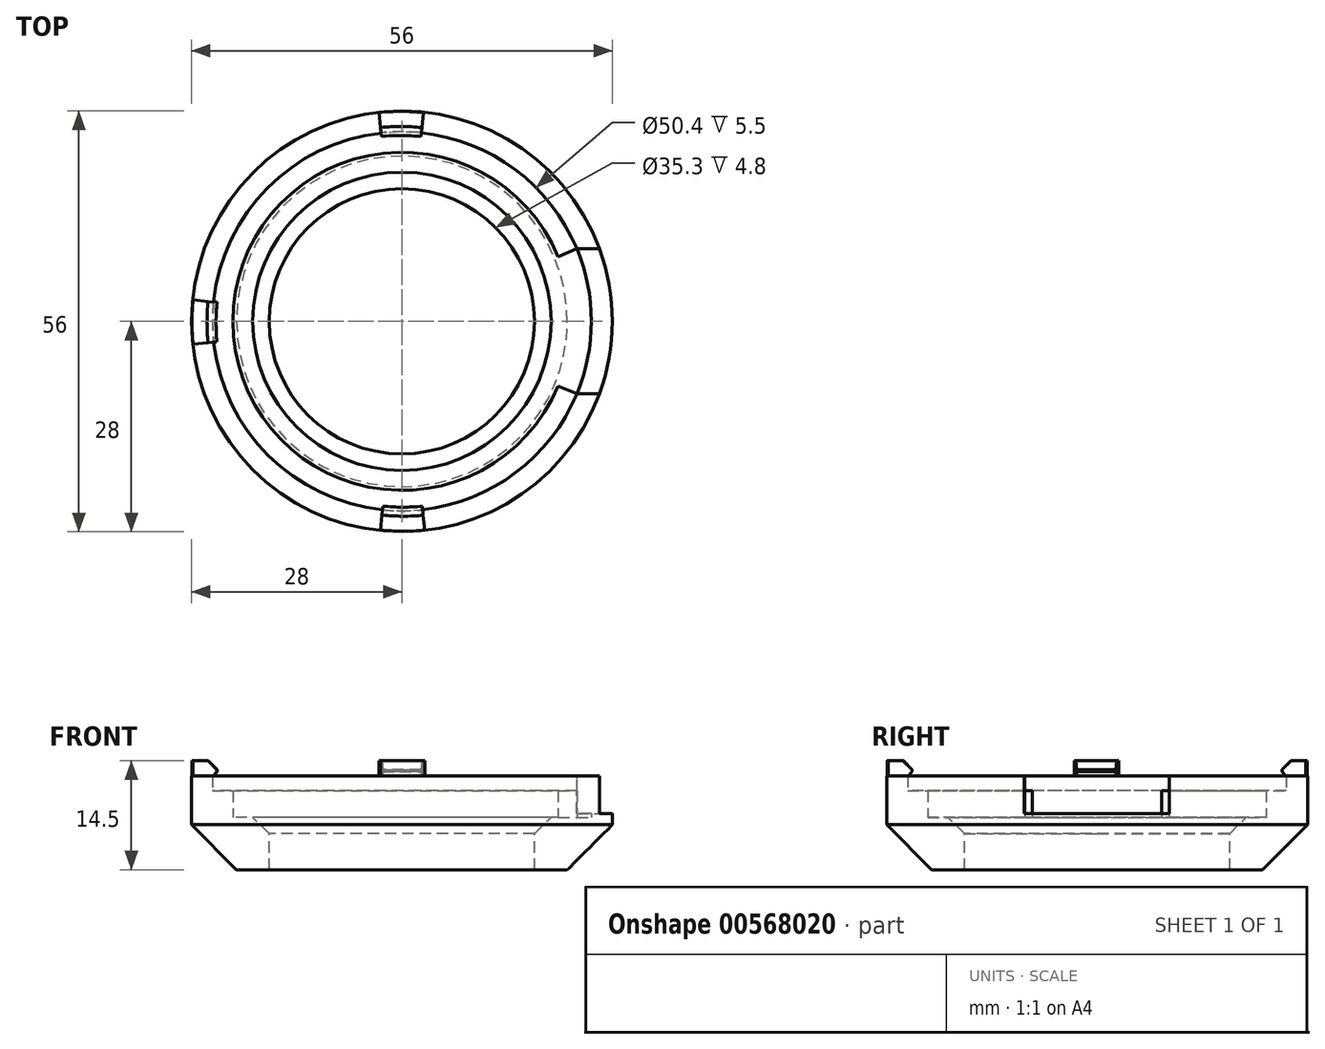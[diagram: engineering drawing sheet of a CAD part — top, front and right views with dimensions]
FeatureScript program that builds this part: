
annotation { "Feature Type Name" : "Feature", "Feature Type Description" : "" }
export const myFeature = defineFeature(function(context is Context, id is Id, definition is map)
    precondition{}
    {
        {
            var Q0;
            Q0=qCreatedBy(makeId("Top.planeOp"),FACE);
            var sketch = newSketch(context, id + "F0", { "sketchPlane" : qUnion([Q0])});
            skArc(sketch, "E0", {"start": v(23.28, 9.64) * mm, "mid": v(-25.2, 0) * mm, "end": v(23.28, -9.64) * mm});
            skArc(sketch, "E1", {"start": v(25.87, 10.72) * mm, "mid": v(-28, 0) * mm, "end": v(25.87, -10.72) * mm});
            skArc(sketch, "E2", {"start": v(16.3, 6.75) * mm, "mid": v(-17.65, 0) * mm, "end": v(16.3, -6.75) * mm});
            skLineSegment(sketch, "E3", {"start": v(0, 0) * mm, "end": v(25.87, 10.72) * mm});
            skLineSegment(sketch, "E4.MirrorCS", {"start": v(0, 0) * mm, "end": v(25.87, -10.72) * mm});
            skCircle(sketch, "E5", {"center": v(0, 0) * mm, "radius": 22.5 * mm});
            skCircle(sketch, "E6", {"center": v(0, 0) * mm, "radius": 17.65 * mm});
            skArc(sketch, "E7", {"start": v(23.28, -9.64) * mm, "mid": v(25.2, 0) * mm, "end": v(23.28, 9.64) * mm});
            skArc(sketch, "E8", {"start": v(25.87, -10.72) * mm, "mid": v(28, 0) * mm, "end": v(25.87, 10.72) * mm});
            skSolve(sketch);
        }
        {
            var Q0;
            Q0=makeQuery(id+"F0.imprint","IMPRINT",FACE,{"disambiguationData":[TD([[makeQuery(id+"F0.imprint","IMPRINT",EDGE,{"derivedFrom":sQuery(id+"F0.wireOp",EDGE,"E0")}),-1.0]])]});
            var Q1;
            {var subQ0=sQuery(id+"F0.wireOp",EDGE,"E7");Q1=makeQuery(id+"F0.imprint","IMPRINT",FACE,{"disambiguationData":[TD([[makeQuery(id+"F0.imprint","IMPRINT",EDGE,{"derivedFrom":subQ0}),-1.0]])]});}
            extrude(context, id + "F1", {"entities" : qUnion([Q0, Q1]), "depth" : 5.5 * mm, "offsetDistance" : 25 * mm, "hasSecondDirection" : true, "secondDirectionOppositeDirection" : true, "secondDirectionDepth" : 7 * mm});
        }
        {
            var Q0;
            Q0=makeQuery(id+"F0.imprint","IMPRINT",FACE,{"disambiguationData":[TD([[makeQuery(id+"F0.imprint","IMPRINT",EDGE,{"derivedFrom":sQuery(id+"F0.wireOp",EDGE,"E0")}),1.0]])]});
            var Q1;
            {var subQ0=sQuery(id+"F0.wireOp",EDGE,"E2");Q1=makeQuery(id+"F0.imprint","IMPRINT",FACE,{"disambiguationData":[TD([[makeQuery(id+"F0.imprint","IMPRINT",EDGE,{"derivedFrom":subQ0}),-1.0]])]});}
            var Q2;
            {var subQ0=sQuery(id+"F0.wireOp",EDGE,"E5");var subQ1=sQuery(id+"F0.wireOp",EDGE,"E3");var subQ2=makeQuery(id+"F0.imprint","INTERSECT",VERTEX,{"derivedFrom":[subQ1,subQ0]});Q2=makeQuery(id+"F0.imprint","IMPRINT",FACE,{"disambiguationData":[TD([[makeQuery(id+"F0.imprint","IMPRINT",EDGE,{"disambiguationData":[TD([[subQ2,1.0]])],"derivedFrom":subQ1}),-1.0]])]});}
            var Q3;
            {var subQ0=sQuery(id+"F0.wireOp",EDGE,"E5");var subQ1=sQuery(id+"F0.wireOp",EDGE,"E3");var subQ2=makeQuery(id+"F0.imprint","INTERSECT",VERTEX,{"derivedFrom":[subQ1,subQ0]});Q3=makeQuery(id+"F0.imprint","IMPRINT",FACE,{"disambiguationData":[TD([[makeQuery(id+"F0.imprint","IMPRINT",EDGE,{"disambiguationData":[TD([[subQ2,1.0]])],"derivedFrom":subQ1}),1.0]])]});}
            var Q4;
            {var subQ0=sQuery(id+"F0.wireOp",EDGE,"E7");Q4=makeQuery(id+"F0.imprint","IMPRINT",FACE,{"disambiguationData":[TD([[makeQuery(id+"F0.imprint","IMPRINT",EDGE,{"derivedFrom":subQ0}),1.0]])]});}
            extrude(context, id + "F2", {"entities" : qUnion([Q0, Q1, Q2, Q3, Q4]), "operationType" : NewBodyOperationType.ADD, "oppositeDirection" : true, "depth" : 7 * mm, "offsetDistance" : 25 * mm});
        }
        {
            var Q0;
            {var subQ0=sQuery(id+"F0.wireOp",EDGE,"E0");Q0=makeQuery(id+"F0.imprint","IMPRINT",FACE,{"disambiguationData":[TD([[makeQuery(id+"F0.imprint","IMPRINT",EDGE,{"derivedFrom":subQ0}),1.0]])]});}
            extrude(context, id + "F3", {"entities" : qUnion([Q0]), "operationType" : NewBodyOperationType.ADD, "depth" : 3.5 * mm, "offsetDistance" : 25 * mm});
        }
        {
            var Q0;
            Q0=makeQuery(id+"F1.opExtrude","CAP_EDGE",EDGE,{"disambiguationData":[OSD([sQuery(id+"F0.wireOp",EDGE,"E1")])],"isStart":true});
            chamfer(context, id + "F4", {"entities" : qUnion([Q0]), "width" : 6 * mm, "tangentPropagation" : true});
        }
        {
            var Q0;
            Q0=makeQuery(id+"F1.opExtrude","CAP_FACE",FACE,{"disambiguationData":[OSD([sQuery(id+"F0.wireOp",EDGE,"E0"),sQuery(id+"F0.wireOp",EDGE,"E1"),sQuery(id+"F0.wireOp",EDGE,"E7"),sQuery(id+"F0.wireOp",EDGE,"E8")])],"isStart":false});
            var sketch = newSketch(context, id + "F5", { "sketchPlane" : qUnion([Q0])});
            skArc(sketch, "E9", {"start": v(26.39, -9.67) * mm, "mid": v(28.15, -0.01) * mm, "end": v(26.4, 9.65) * mm});
            skLineSegment(sketch, "E10", {"start": v(23.28, 9.65) * mm, "end": v(20.75, 8.38) * mm});
            skArc(sketch, "E11", {"start": v(20.68, -8.36) * mm, "mid": v(22.33, 0) * mm, "end": v(20.75, 8.38) * mm});
            skLineSegment(sketch, "E12", {"start": v(20.68, -8.36) * mm, "end": v(23.29, -9.63) * mm});
            skLineSegment(sketch, "E13", {"start": v(23.28, 9.65) * mm, "end": v(26.4, 9.65) * mm});
            skLineSegment(sketch, "E14", {"start": v(23.29, -9.63) * mm, "end": v(26.39, -9.67) * mm});
            skSolve(sketch);
        }
        {
            var Q0;
            {var subQ0=sQuery(id+"F5.wireOp",EDGE,"E11");Q0=makeQuery(id+"F5.imprint","IMPRINT",FACE,{"disambiguationData":[TD([[makeQuery(id+"F5.imprint","IMPRINT",EDGE,{"derivedFrom":subQ0}),-1.0]])]});}
            var Q1;
            {var subQ0=sQuery(id+"F5.wireOp",EDGE,"E10");var subQ4=makeQuery(id+"F1.opExtrude","CAP_EDGE",EDGE,{"disambiguationData":[OSD([sQuery(id+"F0.wireOp",EDGE,"E0"),sQuery(id+"F0.wireOp",EDGE,"E7")])],"isStart":false});var subQ5=makeQuery(id+"F5.imprint","INTERSECT",VERTEX,{"derivedFrom":[subQ4,subQ0]});Q1=makeQuery(id+"F5.imprint","IMPRINT",FACE,{"disambiguationData":[TD([[makeQuery(id+"F5.imprint","IMPRINT",EDGE,{"disambiguationData":[TD([[subQ5,1.0]])],"derivedFrom":subQ0}),1.0]])]});}
            var Q2;
            {var subQ0=sQuery(id+"F5.wireOp",EDGE,"E13");var subQ3=makeQuery(id+"F1.opExtrude","CAP_EDGE",EDGE,{"disambiguationData":[OSD([sQuery(id+"F0.wireOp",EDGE,"E1"),sQuery(id+"F0.wireOp",EDGE,"E8")])],"isStart":false});var subQ4=makeQuery(id+"F5.imprint","INTERSECT",VERTEX,{"derivedFrom":[subQ3,subQ0]});Q2=makeQuery(id+"F5.imprint","IMPRINT",FACE,{"disambiguationData":[TD([[makeQuery(id+"F5.imprint","IMPRINT",EDGE,{"disambiguationData":[TD([[subQ4,1.0]])],"derivedFrom":subQ0}),-1.0]])]});}
            extrude(context, id + "F6", {"entities" : qUnion([Q0, Q1, Q2]), "operationType" : NewBodyOperationType.REMOVE, "oppositeDirection" : true, "depth" : 5 * mm, "offsetDistance" : 25 * mm});
        }
        {
            var Q0;
            Q0=makeQuery(id+"F2.opExtrude","CAP_EDGE",EDGE,{"disambiguationData":[OSD([sQuery(id+"F0.wireOp",EDGE,"E6")])],"isStart":true});
            chamfer(context, id + "F7", {"entities" : qUnion([Q0]), "width" : 2.2 * mm, "tangentPropagation" : true});
        }
        {
            var Q0;
            Q0=makeQuery(id+"F1.opExtrude","CAP_FACE",FACE,{"disambiguationData":[OSD([sQuery(id+"F0.wireOp",EDGE,"E0"),sQuery(id+"F0.wireOp",EDGE,"E1"),sQuery(id+"F0.wireOp",EDGE,"E7"),sQuery(id+"F0.wireOp",EDGE,"E8")])],"isStart":false});
            var sketch = newSketch(context, id + "F8", { "sketchPlane" : qUnion([Q0])});
            skArc(sketch, "E15", {"start": v(-2.52, -24.6) * mm, "mid": v(0.1, -24.74) * mm, "end": v(2.71, -24.61) * mm});
            skArc(sketch, "E16.0", {"start": v(-2.85, -27.78) * mm, "mid": v(0.08, -27.94) * mm, "end": v(3.02, -27.8) * mm});
            skLineSegment(sketch, "E17", {"start": v(-2.52, -24.6) * mm, "end": v(-2.85, -27.78) * mm});
            skLineSegment(sketch, "E18", {"start": v(2.71, -24.61) * mm, "end": v(3.02, -27.8) * mm});
            skSolve(sketch);
        }
        {
            var Q0;
            {var subQ0=sQuery(id+"F8.wireOp",EDGE,"E15");Q0=makeQuery(id+"F8.imprint","IMPRINT",FACE,{"disambiguationData":[TD([[makeQuery(id+"F8.imprint","IMPRINT",EDGE,{"derivedFrom":subQ0}),-1.0]])]});}
            var Q1;
            {var subQ0=sQuery(id+"F8.wireOp",EDGE,"E16.0");Q1=makeQuery(id+"F8.imprint","IMPRINT",FACE,{"disambiguationData":[TD([[makeQuery(id+"F8.imprint","IMPRINT",EDGE,{"derivedFrom":subQ0}),1.0]])]});}
            extrude(context, id + "F9", {"entities" : qUnion([Q0, Q1]), "depth" : 2 * mm, "offsetDistance" : 25 * mm});
        }
        {
            var Q0;
            Q0=makeQuery(id+"F9.opExtrude","CAP_EDGE",EDGE,{"disambiguationData":[OSD([sQuery(id+"F8.wireOp",EDGE,"E15")])],"isStart":true});
            chamfer(context, id + "F10", {"entities" : qUnion([Q0]), "chamferType" : ChamferType.TWO_OFFSETS, "width1" : 0.5 * mm, "oppositeDirection" : false, "width2" : 0.6 * mm, "tangentPropagation" : true});
        }
        {
            var Q0;
            Q0=makeQuery(id+"F9.opExtrude","CAP_EDGE",EDGE,{"disambiguationData":[OSD([sQuery(id+"F8.wireOp",EDGE,"E15")])],"isStart":false});
            chamfer(context, id + "F11", {"entities" : qUnion([Q0]), "width" : 1.2 * mm, "tangentPropagation" : true});
        }
        {
            var Q0;
            Q0=makeQuery(id+"F9.opExtrude","SWEPT_BODY",BODY,{"disambiguationData":[OSD([sQuery(id+"F8.wireOp",EDGE,"E15"),sQuery(id+"F8.wireOp",EDGE,"E16.0"),sQuery(id+"F8.wireOp",EDGE,"E17"),sQuery(id+"F8.wireOp",EDGE,"E18")])]});
            var Q1;
            Q1=makeQuery(id+"F4.opChamfer","BLEND_FACE",FACE,{"disambiguationData":[OSD([sQuery(id+"F0.wireOp",EDGE,"E1"),sQuery(id+"F0.wireOp",EDGE,"E8")])]});
            circularPattern(context, id + "F12", {"operationType" : NewBodyOperationType.ADD, "entities" : qUnion([Q0]), "axis" : qUnion([Q1]), "angle" : 180 * degree, "instanceCount" : 3, "oppositeDirection" : true, "equalSpace" : true});
        }
    });
